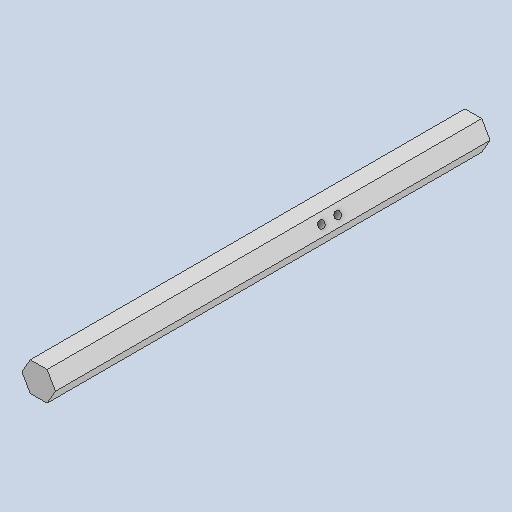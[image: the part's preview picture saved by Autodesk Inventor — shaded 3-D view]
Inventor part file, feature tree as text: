
AUTODESK INVENTOR PART (.ipt)
format: ipt  version: 2022 (Build 260153000, 153)  size: 117,760 bytes
history: native  units: mm
features: other x4, reference x3, extrude x2, sketch x2
ambient origin geometry x8: Origin, YZ Plane, XZ Plane, XY Plane, X Axis, Y Axis, Z Axis, Center Point
bodies: Solid1 (feature_tree)
feature tree (11):
  extrude  "Extrusion1"  Depth=3.1mm TaperAngle=360.0deg
  extrude  "Extrusion3"  Depth=80.0mm
  sketch  "Sketch1"  dims[d0=3.1mm d1=60.0mm d3=360.0deg]
  reference  "Reference1"
  reference  "Reference2"
  sketch  "Sketch2"  dims[d5=80.0mm d6=0.0mm d7=1.3mm d8=49.7mm d9=3.0mm d12=80.0mm d13=0.0mm]
  reference  "Reference3"
  other  "<userpath>\OneDrive\Escritorio\Mini_Proyecto_Diseno\Diseno_18012\Modelo_MPD\caja_nuevo.iam"
  other  "caja_nuevo.iam"
  other  "Rodamiento_Ejes:3"
  other  "hombro_nuevo:8"
